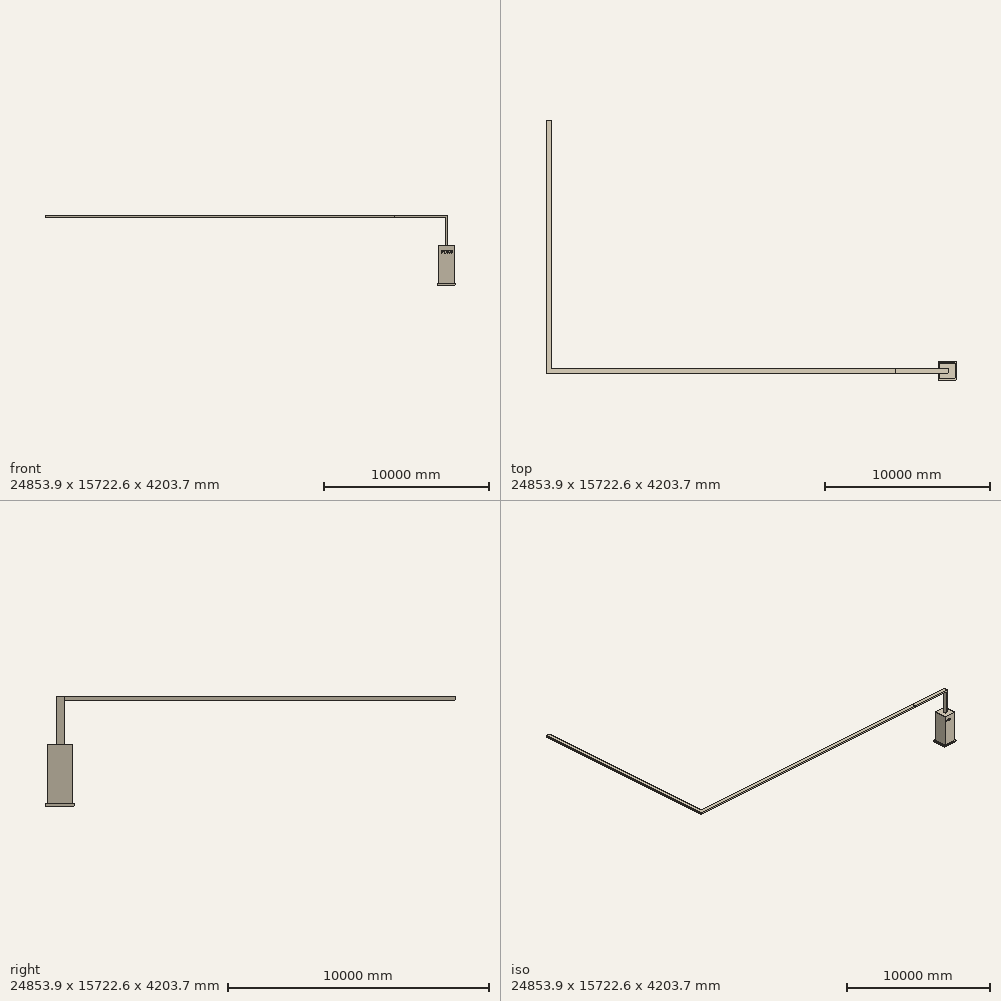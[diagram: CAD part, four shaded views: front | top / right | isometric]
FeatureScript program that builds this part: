
annotation { "Feature Type Name" : "Feature", "Feature Type Description" : "" }
export const myFeature = defineFeature(function(context is Context, id is Id, definition is map)
    precondition{}
    {
        {
            var Q0;
            Q0=qCreatedBy(makeId("Top.planeOp"),FACE);
            var sketch = newSketch(context, id + "F0", { "sketchPlane" : qUnion([Q0])});
            skLineSegment(sketch, "E0.bottom", {"start": v(0, 0) * mm, "end": v(1117.6, 0) * mm});
            skLineSegment(sketch, "E0.top", {"start": v(0, 1117.6) * mm, "end": v(1117.6, 1117.6) * mm});
            skLineSegment(sketch, "E0.left", {"start": v(0, 0) * mm, "end": v(0, 1117.6) * mm});
            skLineSegment(sketch, "E0.right", {"start": v(1117.6, 0) * mm, "end": v(1117.6, 1117.6) * mm});
            skSolve(sketch);
        }
        {
            var Q0;
            Q0=makeQuery(id+"F0.imprint","IMPRINT",FACE,{"disambiguationData":[TD([[makeQuery(id+"F0.imprint","IMPRINT",EDGE,{"derivedFrom":sQuery(id+"F0.wireOp",EDGE,"E0.bottom")}),1.0]])]});
            extrude(context, id + "F1", {"entities" : qUnion([Q0]), "depth" : 88.9 * mm, "offsetDistance" : 25.4 * mm});
        }
        {
            var Q0;
            Q0=makeQuery(id+"F1.opExtrude","CAP_FACE",FACE,{"disambiguationData":[OSD([sQuery(id+"F0.wireOp",EDGE,"E0.bottom"),sQuery(id+"F0.wireOp",EDGE,"E0.top"),sQuery(id+"F0.wireOp",EDGE,"E0.left"),sQuery(id+"F0.wireOp",EDGE,"E0.right")])],"isStart":false});
            var sketch = newSketch(context, id + "F2", { "sketchPlane" : qUnion([Q0])});
            skLineSegment(sketch, "E1.bottom", {"start": v(1041.4, 76.2) * mm, "end": v(76.2, 76.2) * mm});
            skLineSegment(sketch, "E1.top", {"start": v(1041.4, 1041.4) * mm, "end": v(76.2, 1041.4) * mm});
            skLineSegment(sketch, "E1.left", {"start": v(1041.4, 76.2) * mm, "end": v(1041.4, 1041.4) * mm});
            skLineSegment(sketch, "E1.right", {"start": v(76.2, 76.2) * mm, "end": v(76.2, 1041.4) * mm});
            skPoint(sketch, "E1.middle", {"position": v(558.8, 558.8) * mm});
            skPoint(sketch, "E1.middle.positionSnap0", {"position": v(0, 558.8) * mm});
            skPoint(sketch, "E1.middle.positionSnap1", {"position": v(558.8, 0) * mm});
            skPoint(sketch, "E1.centerSnap0", {"position": v(0, 558.8) * mm});
            skPoint(sketch, "E1.centerSnap1", {"position": v(558.8, 0) * mm});
            skSolve(sketch);
        }
        {
            var Q0;
            Q0=makeQuery(id+"F2.imprint","IMPRINT",FACE,{"disambiguationData":[TD([[makeQuery(id+"F2.imprint","IMPRINT",EDGE,{"derivedFrom":sQuery(id+"F2.wireOp",EDGE,"E1.bottom")}),-1.0]])]});
            extrude(context, id + "F3", {"entities" : qUnion([Q0]), "operationType" : NewBodyOperationType.ADD, "depth" : 2286 * mm, "offsetDistance" : 25.4 * mm});
        }
        {
            var Q0;
            Q0=makeQuery(id+"F3.opExtrude","SWEPT_FACE",FACE,{"disambiguationData":[OSD([sQuery(id+"F2.wireOp",EDGE,"E1.bottom")])]});
            var sketch = newSketch(context, id + "F4", { "sketchPlane" : qUnion([Q0])});
            skText(sketch, "E2", { "text": "FRONT", "fontName": "OpenSans-Regular.ttf"});
            const initialGuessF4  = {"E2": [0.12025, 1.90673, 1, 0, 0.19131]};
            skSetInitialGuess(sketch, initialGuessF4);
            skSolve(sketch);
        }
        {
            var Q0;
            Q0 = qSketchRegion(id + "F4", true);
            extrude(context, id + "F5", {"entities" : qUnion([Q0]), "operationType" : NewBodyOperationType.ADD, "depth" : 2.54 * mm, "offsetDistance" : 25.4 * mm});
        }
        {
            var Q0;
            Q0=makeQuery(id+"F3.opExtrude","SWEPT_FACE",FACE,{"disambiguationData":[OSD([sQuery(id+"F2.wireOp",EDGE,"E1.top")])]});
            var sketch = newSketch(context, id + "F6", { "sketchPlane" : qUnion([Q0])});
            skText(sketch, "E3", { "text": "BACK", "fontName": "OpenSans-Regular.ttf"});
            const initialGuessF6  = {"E3": [-1.05277, 1.84864, 1, 0, 0.27433]};
            skSetInitialGuess(sketch, initialGuessF6);
            skSolve(sketch);
        }
        {
            var Q0;
            Q0 = qSketchRegion(id + "F6", true);
            extrude(context, id + "F7", {"entities" : qUnion([Q0]), "operationType" : NewBodyOperationType.ADD, "depth" : 2.54 * mm, "offsetDistance" : 25.4 * mm});
        }
        {
            var Q0;
            Q0=makeQuery(id+"F3.opExtrude","CAP_FACE",FACE,{"disambiguationData":[OSD([sQuery(id+"F2.wireOp",EDGE,"E1.bottom"),sQuery(id+"F2.wireOp",EDGE,"E1.top"),sQuery(id+"F2.wireOp",EDGE,"E1.left"),sQuery(id+"F2.wireOp",EDGE,"E1.right")])],"isStart":false});
            var sketch = newSketch(context, id + "F8", { "sketchPlane" : qUnion([Q0])});
            skLineSegment(sketch, "E4.bottom", {"start": v(622.3, 711.2) * mm, "end": v(495.3, 711.2) * mm});
            skLineSegment(sketch, "E4.top", {"start": v(622.3, 406.4) * mm, "end": v(495.3, 406.4) * mm});
            skLineSegment(sketch, "E4.left", {"start": v(622.3, 711.2) * mm, "end": v(622.3, 406.4) * mm});
            skLineSegment(sketch, "E4.right", {"start": v(495.3, 711.2) * mm, "end": v(495.3, 406.4) * mm});
            skPoint(sketch, "E4.middle", {"position": v(558.8, 558.8) * mm});
            skPoint(sketch, "E4.middle.positionSnap0", {"position": v(76.2, 558.8) * mm});
            skPoint(sketch, "E4.middle.positionSnap1", {"position": v(558.8, 76.2) * mm});
            skPoint(sketch, "E4.centerSnap0", {"position": v(76.2, 558.8) * mm});
            skPoint(sketch, "E4.centerSnap1", {"position": v(558.8, 76.2) * mm});
            skSolve(sketch);
        }
        {
            var Q0;
            Q0=makeQuery(id+"F8.imprint","IMPRINT",FACE,{"disambiguationData":[TD([[makeQuery(id+"F8.imprint","IMPRINT",EDGE,{"derivedFrom":sQuery(id+"F8.wireOp",EDGE,"E4.bottom")}),1.0]])]});
            extrude(context, id + "F9", {"entities" : qUnion([Q0]), "operationType" : NewBodyOperationType.ADD, "depth" : 1828.8 * mm, "offsetDistance" : 25.4 * mm});
        }
        {
            var Q0;
            Q0=makeQuery(id+"F9.opExtrude","SWEPT_FACE",FACE,{"disambiguationData":[OSD([sQuery(id+"F8.wireOp",EDGE,"E4.right")])]});
            var sketch = newSketch(context, id + "F10", { "sketchPlane" : qUnion([Q0])});
            skLineSegment(sketch, "E5.bottom", {"start": v(-711.2, 4203.7) * mm, "end": v(-406.4, 4203.7) * mm});
            skLineSegment(sketch, "E5.top", {"start": v(-711.2, 4076.7) * mm, "end": v(-406.4, 4076.7) * mm});
            skLineSegment(sketch, "E5.left", {"start": v(-711.2, 4203.7) * mm, "end": v(-711.2, 4076.7) * mm});
            skLineSegment(sketch, "E5.right", {"start": v(-406.4, 4203.7) * mm, "end": v(-406.4, 4076.7) * mm});
            skSolve(sketch);
        }
        {
            var Q0;
            Q0=makeQuery(id+"F10.imprint","IMPRINT",FACE,{"disambiguationData":[TD([[makeQuery(id+"F10.imprint","IMPRINT",EDGE,{"derivedFrom":sQuery(id+"F10.wireOp",EDGE,"E5.bottom")}),-1.0]])]});
            extrude(context, id + "F11", {"entities" : qUnion([Q0]), "operationType" : NewBodyOperationType.ADD, "depth" : 3048 * mm, "offsetDistance" : 25.4 * mm});
        }
        {
            var Q0;
            Q0=makeQuery(id+"F11.opExtrude","CAP_FACE",FACE,{"disambiguationData":[OSD([sQuery(id+"F10.wireOp",EDGE,"E5.bottom"),sQuery(id+"F10.wireOp",EDGE,"E5.top"),sQuery(id+"F10.wireOp",EDGE,"E5.left"),sQuery(id+"F10.wireOp",EDGE,"E5.right")])],"isStart":false});
            extrude(context, id + "F12", {"entities" : qUnion([Q0]), "depth" : 67056 * mm, "offsetDistance" : 25.4 * mm});
        }
        {
            var Q0;
            Q0=makeQuery(id+"F12.opExtrude","CAP_FACE",FACE,{"disambiguationData":[OSD([sQuery(id+"F10.wireOp",EDGE,"E5.bottom"),sQuery(id+"F10.wireOp",EDGE,"E5.top"),sQuery(id+"F10.wireOp",EDGE,"E5.left"),sQuery(id+"F10.wireOp",EDGE,"E5.right")])],"isStart":false});
            extrude(context, id + "F13", {"entities" : qUnion([Q0]), "operationType" : NewBodyOperationType.REMOVE, "oppositeDirection" : true, "depth" : 45872.4 * mm, "offsetDistance" : 25.4 * mm});
        }
        {
            var Q0;
            Q0=makeQuery(id+"F12.opExtrude","SWEPT_FACE",FACE,{"disambiguationData":[OSD([sQuery(id+"F10.wireOp",EDGE,"E5.left")])]});
            var sketch = newSketch(context, id + "F14", { "sketchPlane" : qUnion([Q0])});
            skLineSegment(sketch, "E6.bottom", {"start": v(23736.3, 4076.7) * mm, "end": v(23431.5, 4076.7) * mm});
            skLineSegment(sketch, "E6.top", {"start": v(23736.3, 4203.7) * mm, "end": v(23431.5, 4203.7) * mm});
            skLineSegment(sketch, "E6.left", {"start": v(23736.3, 4076.7) * mm, "end": v(23736.3, 4203.7) * mm});
            skLineSegment(sketch, "E6.right", {"start": v(23431.5, 4076.7) * mm, "end": v(23431.5, 4203.7) * mm});
            skSolve(sketch);
        }
        {
            var Q0;
            Q0=makeQuery(id+"F14.imprint","IMPRINT",FACE,{"disambiguationData":[TD([[makeQuery(id+"F14.imprint","IMPRINT",EDGE,{"derivedFrom":sQuery(id+"F14.wireOp",EDGE,"E6.bottom")}),-1.0]])]});
            extrude(context, id + "F15", {"entities" : qUnion([Q0]), "operationType" : NewBodyOperationType.ADD, "depth" : 15011.4 * mm, "offsetDistance" : 25.4 * mm});
        }
    });
